# Revit family: QF_T&S_B-0665-BSTR
name_source: partatom
category: Specialty Equipment
revit_build: Autodesk Revit Architecture 2012 (Build: 20110916_2132(x64)
units: mm (PartAtom-declared; Revit-internal decimal feet)

## types (1)
- QF_T&S_B-0665-BSTR
    Cold Water Connection Height = 0"
    Cold Water Consumption = 12.960 GPM
    Cold Water Flow = 12.96 GPM
    Cold Water Inlet Flow = 12.96 GPM
    Cold Water Maximum Pressure = 125.00 psi
    Cold Water Minimum Pressure = 20.00 psi
    Cold Water RI Height = 0"
    Cold Water Size = 1"
    Cold Water Temperature Recommended = 40 °F
    Description = 8'' Wall Mount Mixing Faucet With Rough Chrome Plated Brass Body, Rough Chrome Plated Brass Spout With Vacuum Breaker, Pail Hook And Garden Hose Male Outlet, Compression Cartridges With Spring Checks, Lever Handles, 1/2'' NPT Female Inlets, Built-In Service Stops In Body And Upper Support Rod
    Foodservice Equipment Identifier = Yes
    Hot Water Connection Height = 0"
    Hot Water Consumption = 12.96 GPM
    Hot Water Flow = 12.96 GPM
    Hot Water Inlet Flow = 12.96 GPM
    Hot Water Maximum Pressure = 125.00 psi
    Hot Water Minimum Pressure = 20.00 psi
    Hot Water RI Height = 0"
    Hot Water Size = 1"
    Hot Water Temperature = 140 °F
    Identify Quantity as Lot = Yes
    Manufacturer = T&S Brass and Bronze Works, Inc.
    Model = B-0665-BSTR
    Plumbing Remarks = Pressure: 20 - 125 psi, Temperature: 40 °F - 140 °F, Flow Rate:  12.96 GPM @ 60 psi
    Product Page URL = http://www.tsbrass.com
    URL = http://www.tsbrass.com
    Water Supply Radius = 1/4"
    Weight in Pounds = 0

## geometry (parser evidence)
native form markers: Blend x10, Sweep x8
no freeform markers — native parametric forms only
